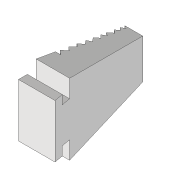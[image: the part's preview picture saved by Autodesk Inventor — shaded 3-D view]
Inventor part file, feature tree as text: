
AUTODESK INVENTOR PART (.ipt)
format: ipt  version: 2020 (Build 240168000, 168)  size: 135,680 bytes
history: native  units: mm
features: extrude x2, sketch x2, other x1
ambient origin geometry x8: Origin, YZ Plane, XZ Plane, XY Plane, X Axis, Y Axis, Z Axis, Center Point
bodies: Volumenkörper1 (feature_tree)
feature tree (5):
  extrude  "Extrusion1"  Depth=20.0mm
  other  "Flächenverjüngung1"
  extrude  "Extrusion2"  Depth=5.0mm
  sketch  "Skizze1"  dims[d0=30.0mm d1=20.0mm]
  sketch  "Skizze2"  dims[d2=5.0mm d3=5.0mm d4=50.0mm d5=13.962634mm d6=40.0mm d7=10.0mm d8=0.0mm d9=1.745329mm d10=3.082mm d11=0.0mm]
